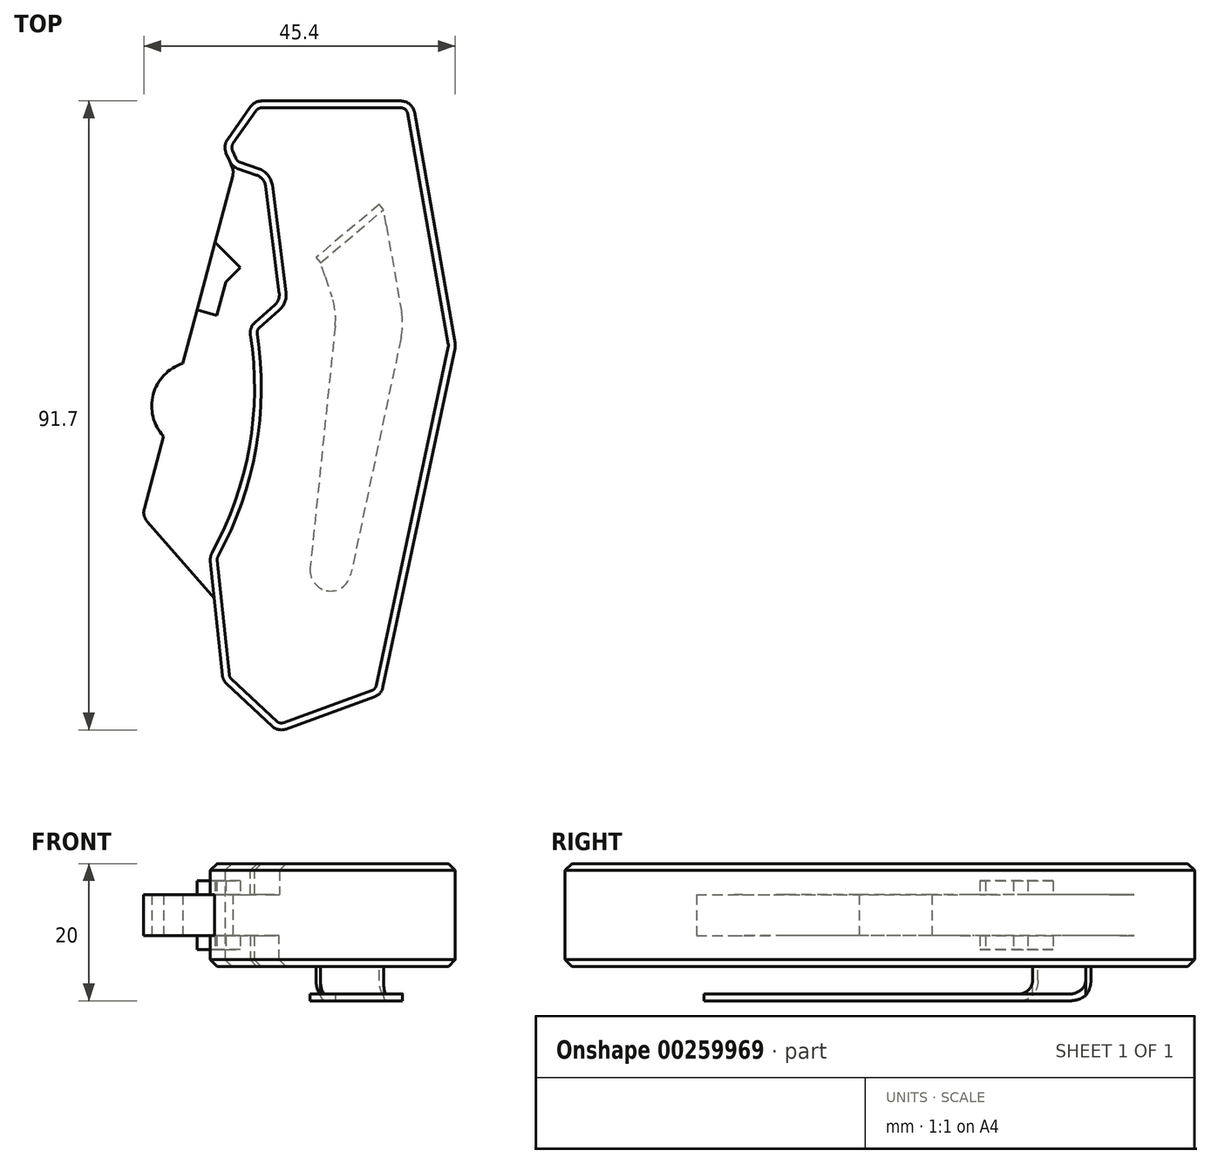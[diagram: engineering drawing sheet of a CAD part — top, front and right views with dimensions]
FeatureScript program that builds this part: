
annotation { "Feature Type Name" : "Feature", "Feature Type Description" : "" }
export const myFeature = defineFeature(function(context is Context, id is Id, definition is map)
    precondition{}
    {
        {
            var Q0;
            Q0=qCreatedBy(makeId("Top.planeOp"),FACE);
            var sketch = newSketch(context, id + "F0", { "sketchPlane" : qUnion([Q0])});
            skLineSegment(sketch, "E0", {"start": v(0, 0) * mm, "end": v(15.04, 5.47) * mm});
            skLineSegment(sketch, "E1", {"start": v(0, 0) * mm, "end": v(-8.04, 7.5) * mm});
            skLineSegment(sketch, "E2", {"start": v(-8.04, 7.5) * mm, "end": v(-9.3, 19.44) * mm});
            skLineSegment(sketch, "E3", {"start": v(-9.3, 19.44) * mm, "end": v(-19.8, 31.51) * mm});
            skLineSegment(sketch, "E4", {"start": v(-3.44, 92) * mm, "end": v(19.56, 92) * mm});
            skLineSegment(sketch, "E5", {"start": v(19.56, 92) * mm, "end": v(25.85, 56.34) * mm});
            skLineSegment(sketch, "E6", {"start": v(25.85, 56.34) * mm, "end": v(15.04, 5.47) * mm});
            skLineSegment(sketch, "E7", {"start": v(-3.44, 92) * mm, "end": v(-8.03, 85.45) * mm});
            skLineSegment(sketch, "E8", {"start": v(-8.03, 85.45) * mm, "end": v(-6.45, 81.77) * mm});
            skLineSegment(sketch, "E9", {"start": v(-6.45, 81.77) * mm, "end": v(-19.8, 31.51) * mm});
            skArc(sketch, "E10", {"start": v(-13.9, 53.74) * mm, "mid": v(-18.2, 49.2) * mm, "end": v(-16.72, 43.1) * mm});
            skSolve(sketch);
        }
        {
            var Q0;
            Q0 = qSketchRegion(id + "F0", true);
            extrude(context, id + "F1", {"entities" : qUnion([Q0]), "depth" : 15 * mm});
        }
        {
            var Q0;
            Q0=makeQuery(id+"F1.opExtrude","SWEPT_EDGE",EDGE,{"disambiguationData":[OSD([sQuery(id+"F0.wireOp",EDGE,"E4"),sQuery(id+"F0.wireOp",EDGE,"E7")])]});
            var Q1;
            Q1=makeQuery(id+"F1.opExtrude","SWEPT_EDGE",EDGE,{"disambiguationData":[OSD([sQuery(id+"F0.wireOp",EDGE,"E4"),sQuery(id+"F0.wireOp",EDGE,"E5")])]});
            var Q2;
            Q2=makeQuery(id+"F1.opExtrude","SWEPT_EDGE",EDGE,{"disambiguationData":[OSD([sQuery(id+"F0.wireOp",EDGE,"E7"),sQuery(id+"F0.wireOp",EDGE,"E8")])]});
            var Q3;
            Q3=makeQuery(id+"F1.opExtrude","SWEPT_EDGE",EDGE,{"disambiguationData":[OSD([sQuery(id+"F0.wireOp",EDGE,"E8"),sQuery(id+"F0.wireOp",EDGE,"E9")])]});
            var Q4;
            Q4=makeQuery(id+"F1.opExtrude","SWEPT_EDGE",EDGE,{"disambiguationData":[OSD([sQuery(id+"F0.wireOp",EDGE,"E5"),sQuery(id+"F0.wireOp",EDGE,"E6")])]});
            var Q5;
            Q5=makeQuery(id+"F1.opExtrude","SWEPT_EDGE",EDGE,{"disambiguationData":[OSD([sQuery(id+"F0.wireOp",EDGE,"E0"),sQuery(id+"F0.wireOp",EDGE,"E6")])]});
            var Q6;
            Q6=makeQuery(id+"F1.opExtrude","SWEPT_EDGE",EDGE,{"disambiguationData":[OSD([sQuery(id+"F0.wireOp",EDGE,"E3"),sQuery(id+"F0.wireOp",EDGE,"E9")])]});
            var Q7;
            Q7=makeQuery(id+"F1.opExtrude","SWEPT_EDGE",EDGE,{"disambiguationData":[OSD([sQuery(id+"F0.wireOp",EDGE,"E1"),sQuery(id+"F0.wireOp",EDGE,"E2")])]});
            var Q8;
            Q8=makeQuery(id+"F1.opExtrude","SWEPT_EDGE",EDGE,{"disambiguationData":[OSD([sQuery(id+"F0.wireOp",EDGE,"E0"),sQuery(id+"F0.wireOp",EDGE,"E1")])]});
            fillet(context, id + "F2", {"entities" : qUnion([Q0, Q1, Q2, Q3, Q4, Q5, Q6, Q7, Q8]), "radius" : 2 * mm, "tangentPropagation" : true, "allowEdgeOverflow" : false});
        }
        {
            var Q0;
            Q0=makeQuery(id+"F1.opExtrude","CAP_FACE",FACE,{"disambiguationData":[OSD([sQuery(id+"F0.wireOp",EDGE,"E0"),sQuery(id+"F0.wireOp",EDGE,"E1"),sQuery(id+"F0.wireOp",EDGE,"E2"),sQuery(id+"F0.wireOp",EDGE,"E3"),sQuery(id+"F0.wireOp",EDGE,"E4"),sQuery(id+"F0.wireOp",EDGE,"E5"),sQuery(id+"F0.wireOp",EDGE,"E6"),sQuery(id+"F0.wireOp",EDGE,"E7"),sQuery(id+"F0.wireOp",EDGE,"E8"),sQuery(id+"F0.wireOp",EDGE,"E9"),sQuery(id+"F0.wireOp",EDGE,"E10")])],"isStart":false});
            var sketch = newSketch(context, id + "F3", { "sketchPlane" : qUnion([Q0])});
            skLineSegment(sketch, "E11", {"start": v(-9.3, 19.44) * mm, "end": v(-9.94, 25.56) * mm});
            skLineSegment(sketch, "E12", {"start": v(-6.73, 82.4) * mm, "end": v(-2, 80.8) * mm});
            skLineSegment(sketch, "E13", {"start": v(-2, 80.8) * mm, "end": v(0.28, 62.94) * mm});
            skLineSegment(sketch, "E14", {"start": v(0.28, 62.94) * mm, "end": v(-4.23, 58.98) * mm});
            skArc(sketch, "E15", {"start": v(-9.94, 25.56) * mm, "mid": v(-4.17, 41.77) * mm, "end": v(-4.23, 58.98) * mm});
            skSolve(sketch);
        }
        {
            var Q0;
            Q0=makeQuery(id+"F3.imprint","IMPRINT",FACE,{"disambiguationData":[TD([[makeQuery(id+"F3.imprint","IMPRINT",EDGE,{"derivedFrom":sQuery(id+"F3.wireOp",EDGE,"E11")}),1.0]])]});
            extrude(context, id + "F4", {"entities" : qUnion([Q0]), "operationType" : NewBodyOperationType.REMOVE, "oppositeDirection" : true, "depth" : 4.5 * mm});
        }
        {
            var Q0;
            Q0=makeQuery(id+"F1.opExtrude","CAP_FACE",FACE,{"disambiguationData":[OSD([sQuery(id+"F0.wireOp",EDGE,"E0"),sQuery(id+"F0.wireOp",EDGE,"E1"),sQuery(id+"F0.wireOp",EDGE,"E2"),sQuery(id+"F0.wireOp",EDGE,"E3"),sQuery(id+"F0.wireOp",EDGE,"E4"),sQuery(id+"F0.wireOp",EDGE,"E5"),sQuery(id+"F0.wireOp",EDGE,"E6"),sQuery(id+"F0.wireOp",EDGE,"E7"),sQuery(id+"F0.wireOp",EDGE,"E8"),sQuery(id+"F0.wireOp",EDGE,"E9"),sQuery(id+"F0.wireOp",EDGE,"E10")])],"isStart":true});
            var sketch = newSketch(context, id + "F5", { "sketchPlane" : qUnion([Q0])});
            skLineSegment(sketch, "E16", {"start": v(0, 1.25) * mm, "end": v(0, -26.47) * mm, "construction": true});
            skLineSegment(sketch, "E17.MirrorCS", {"start": v(-6.73, -82.4) * mm, "end": v(-2, -80.75) * mm});
            skLineSegment(sketch, "E18.MirrorCS", {"start": v(-2, -80.75) * mm, "end": v(0.27, -62.9) * mm});
            skLineSegment(sketch, "E19.MirrorCS", {"start": v(-9.3, -19.44) * mm, "end": v(-9.94, -25.56) * mm});
            skLineSegment(sketch, "E20.MirrorCS", {"start": v(0.27, -62.9) * mm, "end": v(-4.24, -58.94) * mm});
            skArc(sketch, "E21.MirrorCS", {"start": v(-9.94, -25.56) * mm, "mid": v(-4.18, -41.75) * mm, "end": v(-4.24, -58.94) * mm});
            skSolve(sketch);
        }
        {
            var Q0;
            Q0=makeQuery(id+"F5.imprint","IMPRINT",FACE,{"disambiguationData":[TD([[makeQuery(id+"F5.imprint","IMPRINT",EDGE,{"derivedFrom":sQuery(id+"F5.wireOp",EDGE,"E17.MirrorCS")}),1.0]])]});
            extrude(context, id + "F6", {"entities" : qUnion([Q0]), "operationType" : NewBodyOperationType.REMOVE, "oppositeDirection" : true, "depth" : 4.5 * mm});
        }
        {
            var Q0;
            Q0=makeQuery(id+"F4.boolean.opBoolean","COPY",EDGE,{"derivedFrom":makeQuery(id+"F4.opExtrude","SWEPT_EDGE",EDGE,{"disambiguationData":[OSD([sQuery(id+"F3.wireOp",EDGE,"E11"),sQuery(id+"F3.wireOp",EDGE,"E15")])]})});
            var Q1;
            Q1=makeQuery(id+"F6.boolean.opBoolean","COPY",EDGE,{"derivedFrom":makeQuery(id+"F6.opExtrude","SWEPT_EDGE",EDGE,{"disambiguationData":[OSD([sQuery(id+"F5.wireOp",EDGE,"E19.MirrorCS"),sQuery(id+"F5.wireOp",EDGE,"E21.MirrorCS")])]})});
            var Q2;
            Q2=makeQuery(id+"F4.boolean.opBoolean","COPY",EDGE,{"derivedFrom":makeQuery(id+"F4.opExtrude","SWEPT_EDGE",EDGE,{"disambiguationData":[OSD([sQuery(id+"F3.wireOp",EDGE,"E14"),sQuery(id+"F3.wireOp",EDGE,"E15")])]})});
            var Q3;
            Q3=makeQuery(id+"F4.boolean.opBoolean","COPY",EDGE,{"derivedFrom":makeQuery(id+"F4.opExtrude","SWEPT_EDGE",EDGE,{"disambiguationData":[OSD([sQuery(id+"F3.wireOp",EDGE,"E13"),sQuery(id+"F3.wireOp",EDGE,"E14")])]})});
            var Q4;
            Q4=makeQuery(id+"F6.boolean.opBoolean","COPY",EDGE,{"derivedFrom":makeQuery(id+"F6.opExtrude","SWEPT_EDGE",EDGE,{"disambiguationData":[OSD([sQuery(id+"F5.wireOp",EDGE,"E20.MirrorCS"),sQuery(id+"F5.wireOp",EDGE,"E21.MirrorCS")])]})});
            var Q5;
            Q5=makeQuery(id+"F6.boolean.opBoolean","COPY",EDGE,{"derivedFrom":makeQuery(id+"F6.opExtrude","SWEPT_EDGE",EDGE,{"disambiguationData":[OSD([sQuery(id+"F5.wireOp",EDGE,"E18.MirrorCS"),sQuery(id+"F5.wireOp",EDGE,"E20.MirrorCS")])]})});
            var Q6;
            Q6=makeQuery(id+"F4.boolean.opBoolean","COPY",EDGE,{"derivedFrom":makeQuery(id+"F4.opExtrude","SWEPT_EDGE",EDGE,{"disambiguationData":[OSD([sQuery(id+"F3.wireOp",EDGE,"E12"),sQuery(id+"F3.wireOp",EDGE,"E13")])]})});
            var Q7;
            Q7=makeQuery(id+"F6.boolean.opBoolean","COPY",EDGE,{"derivedFrom":makeQuery(id+"F6.opExtrude","SWEPT_EDGE",EDGE,{"disambiguationData":[OSD([sQuery(id+"F5.wireOp",EDGE,"E17.MirrorCS"),sQuery(id+"F5.wireOp",EDGE,"E18.MirrorCS")])]})});
            var Q8;
            {var subQ0=sQuery(id+"F0.wireOp",EDGE,"E9");var subQ1=sQuery(id+"F0.wireOp",EDGE,"E8");Q8=makeQuery(id+"F4.boolean.opBoolean","MERGE",EDGE,{"derivedFrom":[makeQuery(id+"F2.opFillet","BLEND_EDGE",EDGE,{"blendedFrom":[makeQuery(id+"F1.opExtrude","SWEPT_EDGE",EDGE,{"disambiguationData":[OSD([subQ1,subQ0])]}),makeQuery(id+"F1.opExtrude","SWEPT_FACE",FACE,{"disambiguationData":[OSD([subQ1])]})],"blendedInto":[makeQuery(id+"F1.opExtrude","SWEPT_FACE",FACE,{"disambiguationData":[OSD([subQ1])]})]}),makeQuery(id+"F4.opExtrude","SWEPT_EDGE",EDGE,{"disambiguationData":[OSD([sQuery(id+"F0.wireOp",EDGE,"E0"),sQuery(id+"F0.wireOp",EDGE,"E1"),sQuery(id+"F0.wireOp",EDGE,"E2"),sQuery(id+"F0.wireOp",EDGE,"E3"),sQuery(id+"F0.wireOp",EDGE,"E4"),sQuery(id+"F0.wireOp",EDGE,"E5"),sQuery(id+"F0.wireOp",EDGE,"E6"),sQuery(id+"F0.wireOp",EDGE,"E7"),subQ1,subQ0,sQuery(id+"F0.wireOp",EDGE,"E10"),sQuery(id+"F3.wireOp",EDGE,"E12")])]})]});}
            var Q9;
            {var subQ0=sQuery(id+"F0.wireOp",EDGE,"E9");var subQ1=sQuery(id+"F0.wireOp",EDGE,"E8");Q9=makeQuery(id+"F6.boolean.opBoolean","MERGE",EDGE,{"derivedFrom":[makeQuery(id+"F4.boolean.opBoolean","SPLIT",EDGE,{"derivedFrom":makeQuery(id+"F2.opFillet","BLEND_EDGE",EDGE,{"blendedFrom":[makeQuery(id+"F1.opExtrude","SWEPT_EDGE",EDGE,{"disambiguationData":[OSD([subQ1,subQ0])]}),makeQuery(id+"F1.opExtrude","SWEPT_FACE",FACE,{"disambiguationData":[OSD([subQ1])]})],"blendedInto":[makeQuery(id+"F1.opExtrude","SWEPT_FACE",FACE,{"disambiguationData":[OSD([subQ1])]})]})}),makeQuery(id+"F6.opExtrude","SWEPT_EDGE",EDGE,{"disambiguationData":[OSD([sQuery(id+"F0.wireOp",EDGE,"E0"),sQuery(id+"F0.wireOp",EDGE,"E1"),sQuery(id+"F0.wireOp",EDGE,"E2"),sQuery(id+"F0.wireOp",EDGE,"E3"),sQuery(id+"F0.wireOp",EDGE,"E4"),sQuery(id+"F0.wireOp",EDGE,"E5"),sQuery(id+"F0.wireOp",EDGE,"E6"),sQuery(id+"F0.wireOp",EDGE,"E7"),subQ1,subQ0,sQuery(id+"F0.wireOp",EDGE,"E10"),sQuery(id+"F5.wireOp",EDGE,"E17.MirrorCS")])]})]});}
            fillet(context, id + "F7", {"entities" : qUnion([Q0, Q1, Q2, Q3, Q4, Q5, Q6, Q7, Q8, Q9]), "radius" : 2 * mm, "tangentPropagation" : true, "allowEdgeOverflow" : false});
        }
        {
            var Q0;
            Q0=makeQuery(id+"F1.opExtrude","CAP_FACE",FACE,{"disambiguationData":[OSD([sQuery(id+"F0.wireOp",EDGE,"E0"),sQuery(id+"F0.wireOp",EDGE,"E1"),sQuery(id+"F0.wireOp",EDGE,"E2"),sQuery(id+"F0.wireOp",EDGE,"E3"),sQuery(id+"F0.wireOp",EDGE,"E4"),sQuery(id+"F0.wireOp",EDGE,"E5"),sQuery(id+"F0.wireOp",EDGE,"E6"),sQuery(id+"F0.wireOp",EDGE,"E7"),sQuery(id+"F0.wireOp",EDGE,"E8"),sQuery(id+"F0.wireOp",EDGE,"E9"),sQuery(id+"F0.wireOp",EDGE,"E10")])],"isStart":false});
            var Q1;
            Q1=makeQuery(id+"F1.opExtrude","CAP_FACE",FACE,{"disambiguationData":[OSD([sQuery(id+"F0.wireOp",EDGE,"E0"),sQuery(id+"F0.wireOp",EDGE,"E1"),sQuery(id+"F0.wireOp",EDGE,"E2"),sQuery(id+"F0.wireOp",EDGE,"E3"),sQuery(id+"F0.wireOp",EDGE,"E4"),sQuery(id+"F0.wireOp",EDGE,"E5"),sQuery(id+"F0.wireOp",EDGE,"E6"),sQuery(id+"F0.wireOp",EDGE,"E7"),sQuery(id+"F0.wireOp",EDGE,"E8"),sQuery(id+"F0.wireOp",EDGE,"E9"),sQuery(id+"F0.wireOp",EDGE,"E10")])],"isStart":true});
            chamfer(context, id + "F8", {"entities" : qUnion([Q0, Q1]), "width" : 1 * mm, "tangentPropagation" : true});
        }
        {
            var Q0;
            Q0=makeQuery(id+"F4.boolean.opBoolean","COPY",FACE,{"derivedFrom":makeQuery(id+"F4.opExtrude","CAP_FACE",FACE,{"disambiguationData":[OSD([sQuery(id+"F0.wireOp",EDGE,"E0"),sQuery(id+"F0.wireOp",EDGE,"E1"),sQuery(id+"F0.wireOp",EDGE,"E2"),sQuery(id+"F0.wireOp",EDGE,"E3"),sQuery(id+"F0.wireOp",EDGE,"E4"),sQuery(id+"F0.wireOp",EDGE,"E5"),sQuery(id+"F0.wireOp",EDGE,"E6"),sQuery(id+"F0.wireOp",EDGE,"E7"),sQuery(id+"F0.wireOp",EDGE,"E8"),sQuery(id+"F0.wireOp",EDGE,"E9"),sQuery(id+"F0.wireOp",EDGE,"E10"),sQuery(id+"F3.wireOp",EDGE,"E11"),sQuery(id+"F3.wireOp",EDGE,"E12"),sQuery(id+"F3.wireOp",EDGE,"E13"),sQuery(id+"F3.wireOp",EDGE,"E14"),sQuery(id+"F3.wireOp",EDGE,"E15")])],"isStart":false})});
            var sketch = newSketch(context, id + "F9", { "sketchPlane" : qUnion([Q0])});
            skLineSegment(sketch, "E22", {"start": v(-11.83, 61.53) * mm, "end": v(-8.93, 60.76) * mm});
            skLineSegment(sketch, "E23", {"start": v(-8.93, 60.76) * mm, "end": v(-7.65, 65.59) * mm});
            skLineSegment(sketch, "E24", {"start": v(-7.65, 65.59) * mm, "end": v(-5.53, 67.71) * mm});
            skPoint(sketch, "E25.end.orphan", {"position": v(-14.92, 77.49) * mm});
            skLineSegment(sketch, "E26", {"start": v(-5.53, 67.71) * mm, "end": v(-9.21, 71.38) * mm});
            skLineSegment(sketch, "E27", {"start": v(-11.83, 61.53) * mm, "end": v(-9.21, 71.38) * mm});
            skSolve(sketch);
        }
        {
            var Q0;
            Q0 = qSketchRegion(id + "F9", true);
            extrude(context, id + "F10", {"entities" : qUnion([Q0]), "operationType" : NewBodyOperationType.ADD, "depth" : 2 * mm, "hasSecondDirection" : true, "secondDirectionOppositeDirection" : true, "secondDirectionDepth" : 8 * mm});
        }
        {
            var Q0;
            Q0=makeQuery(id+"F1.opExtrude","CAP_FACE",FACE,{"disambiguationData":[OSD([sQuery(id+"F0.wireOp",EDGE,"E0"),sQuery(id+"F0.wireOp",EDGE,"E1"),sQuery(id+"F0.wireOp",EDGE,"E2"),sQuery(id+"F0.wireOp",EDGE,"E3"),sQuery(id+"F0.wireOp",EDGE,"E4"),sQuery(id+"F0.wireOp",EDGE,"E5"),sQuery(id+"F0.wireOp",EDGE,"E6"),sQuery(id+"F0.wireOp",EDGE,"E7"),sQuery(id+"F0.wireOp",EDGE,"E8"),sQuery(id+"F0.wireOp",EDGE,"E9"),sQuery(id+"F0.wireOp",EDGE,"E10")])],"isStart":true});
            var sketch = newSketch(context, id + "F11", { "sketchPlane" : qUnion([Q0])});
            skLineSegment(sketch, "E28", {"start": v(14.7, -76.9) * mm, "end": v(5.52, -69.19) * mm});
            skLineSegment(sketch, "E29", {"start": v(5.52, -69.19) * mm, "end": v(6.16, -68.42) * mm});
            skLineSegment(sketch, "E30", {"start": v(6.16, -68.42) * mm, "end": v(15.35, -76.13) * mm});
            skLineSegment(sketch, "E31", {"start": v(15.35, -76.13) * mm, "end": v(14.7, -76.9) * mm});
            skSolve(sketch);
        }
        {
            var Q0;
            Q0 = qSketchRegion(id + "F11", true);
            extrude(context, id + "F12", {"entities" : qUnion([Q0]), "operationType" : NewBodyOperationType.ADD, "depth" : 5 * mm, "offsetDistance" : 25 * mm});
        }
        {
            var Q0;
            Q0=makeQuery(id+"F12.opExtrude","CAP_FACE",FACE,{"disambiguationData":[OSD([sQuery(id+"F11.wireOp",EDGE,"E28"),sQuery(id+"F11.wireOp",EDGE,"E29"),sQuery(id+"F11.wireOp",EDGE,"E30"),sQuery(id+"F11.wireOp",EDGE,"E31")])],"isStart":false});
            var sketch = newSketch(context, id + "F13", { "sketchPlane" : qUnion([Q0])});
            skLineSegment(sketch, "E32", {"start": v(15.35, -76.13) * mm, "end": v(18.3, -59.36) * mm});
            skLineSegment(sketch, "E33", {"start": v(18.3, -59.36) * mm, "end": v(9.94, -20) * mm});
            skLineSegment(sketch, "E34", {"start": v(6.16, -68.42) * mm, "end": v(8.53, -61.38) * mm});
            skLineSegment(sketch, "E35", {"start": v(8.53, -61.38) * mm, "end": v(4.37, -21.18) * mm});
            skLineSegment(sketch, "E36", {"start": v(4.37, -21.18) * mm, "end": v(9.94, -20) * mm});
            skSolve(sketch);
        }
        {
            var Q0;
            Q0=makeQuery(id+"F13.imprint","IMPRINT",FACE,{"disambiguationData":[TD([[makeQuery(id+"F13.imprint","IMPRINT",EDGE,{"derivedFrom":sQuery(id+"F13.wireOp",EDGE,"E32")}),1.0]])]});
            var Q1;
            Q1=makeQuery(id+"F13.imprint","IMPRINT",FACE,{"disambiguationData":[TD([[makeQuery(id+"F13.imprint","IMPRINT",EDGE,{"derivedFrom":makeQuery(id+"F12.opExtrude","CAP_EDGE",EDGE,{"disambiguationData":[OSD([sQuery(id+"F11.wireOp",EDGE,"E28")])],"isStart":false})}),-1.0]])]});
            extrude(context, id + "F14", {"entities" : qUnion([Q0, Q1]), "operationType" : NewBodyOperationType.ADD, "oppositeDirection" : true, "depth" : 1 * mm, "offsetDistance" : 25 * mm});
        }
        {
            var Q0;
            Q0=makeQuery(id+"F14.opExtrude","SWEPT_EDGE",EDGE,{"disambiguationData":[OSD([sQuery(id+"F13.wireOp",EDGE,"E32"),sQuery(id+"F13.wireOp",EDGE,"E33")])]});
            var Q1;
            Q1=makeQuery(id+"F14.opExtrude","SWEPT_EDGE",EDGE,{"disambiguationData":[OSD([sQuery(id+"F13.wireOp",EDGE,"E34"),sQuery(id+"F13.wireOp",EDGE,"E35")])]});
            fillet(context, id + "F15", {"entities" : qUnion([Q0, Q1]), "radius" : 10 * mm, "tangentPropagation" : true, "allowEdgeOverflow" : false});
        }
        {
            var Q0;
            Q0=makeQuery(id+"F14.opExtrude","SWEPT_EDGE",EDGE,{"disambiguationData":[OSD([sQuery(id+"F13.wireOp",EDGE,"E35"),sQuery(id+"F13.wireOp",EDGE,"E36")])]});
            var Q1;
            Q1=makeQuery(id+"F14.opExtrude","SWEPT_EDGE",EDGE,{"disambiguationData":[OSD([sQuery(id+"F13.wireOp",EDGE,"E33"),sQuery(id+"F13.wireOp",EDGE,"E36")])]});
            fillet(context, id + "F16", {"entities" : qUnion([Q0, Q1]), "radius" : 3 * mm, "tangentPropagation" : true, "allowEdgeOverflow" : false});
        }
        {
            var Q0;
            Q0=makeQuery(id+"F14.boolean.opBoolean","INTERSECT",EDGE,{"derivedFrom":[makeQuery(id+"F12.opExtrude","SWEPT_FACE",FACE,{"disambiguationData":[OSD([sQuery(id+"F11.wireOp",EDGE,"E30")])]}),makeQuery(id+"F14.opExtrude","CAP_FACE",FACE,{"disambiguationData":[OSD([sQuery(id+"F11.wireOp",EDGE,"E28"),sQuery(id+"F11.wireOp",EDGE,"E29"),sQuery(id+"F11.wireOp",EDGE,"E31"),sQuery(id+"F13.wireOp",EDGE,"E32"),sQuery(id+"F13.wireOp",EDGE,"E33"),sQuery(id+"F13.wireOp",EDGE,"E34"),sQuery(id+"F13.wireOp",EDGE,"E35"),sQuery(id+"F13.wireOp",EDGE,"E36")])],"isStart":false})]});
            fillet(context, id + "F17", {"entities" : qUnion([Q0]), "radius" : 2 * mm, "tangentPropagation" : true, "allowEdgeOverflow" : false});
        }
        {
            var Q0;
            Q0=makeQuery(id+"F12.opExtrude","CAP_EDGE",EDGE,{"disambiguationData":[OSD([sQuery(id+"F11.wireOp",EDGE,"E28")])],"isStart":false});
            fillet(context, id + "F18", {"entities" : qUnion([Q0]), "radius" : 3 * mm, "tangentPropagation" : true, "allowEdgeOverflow" : false});
        }
    });
